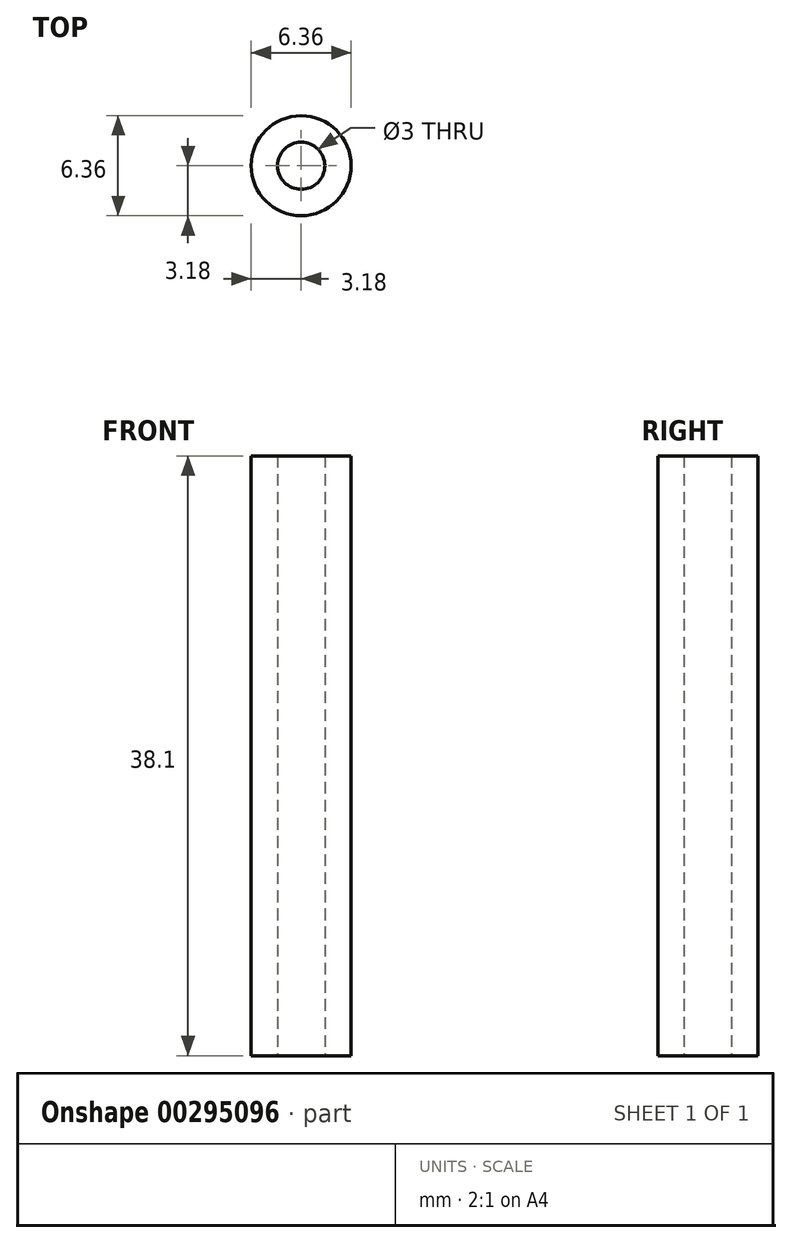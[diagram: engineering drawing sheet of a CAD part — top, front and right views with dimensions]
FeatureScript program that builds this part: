
annotation { "Feature Type Name" : "Feature", "Feature Type Description" : "" }
export const myFeature = defineFeature(function(context is Context, id is Id, definition is map)
    precondition{}
    {
        {
            var Q0;
            Q0=qCreatedBy(makeId("Top.planeOp"),FACE);
            var sketch = newSketch(context, id + "F0", { "sketchPlane" : qUnion([Q0])});
            skCircle(sketch, "E0", {"center": v(0, 0) * mm, "radius": 3.18 * mm});
            skCircle(sketch, "E1", {"center": v(0, 0) * mm, "radius": 1.5 * mm});
            skSolve(sketch);
        }
        {
            var Q0;
            Q0=makeQuery(id+"F0.imprint","IMPRINT",FACE,{"disambiguationData":[TD([[makeQuery(id+"F0.imprint","IMPRINT",EDGE,{"derivedFrom":sQuery(id+"F0.wireOp",EDGE,"E0")}),1.0]])]});
            extrude(context, id + "F1", {"entities" : qUnion([Q0]), "depth" : 38.1 * mm});
        }
    });
